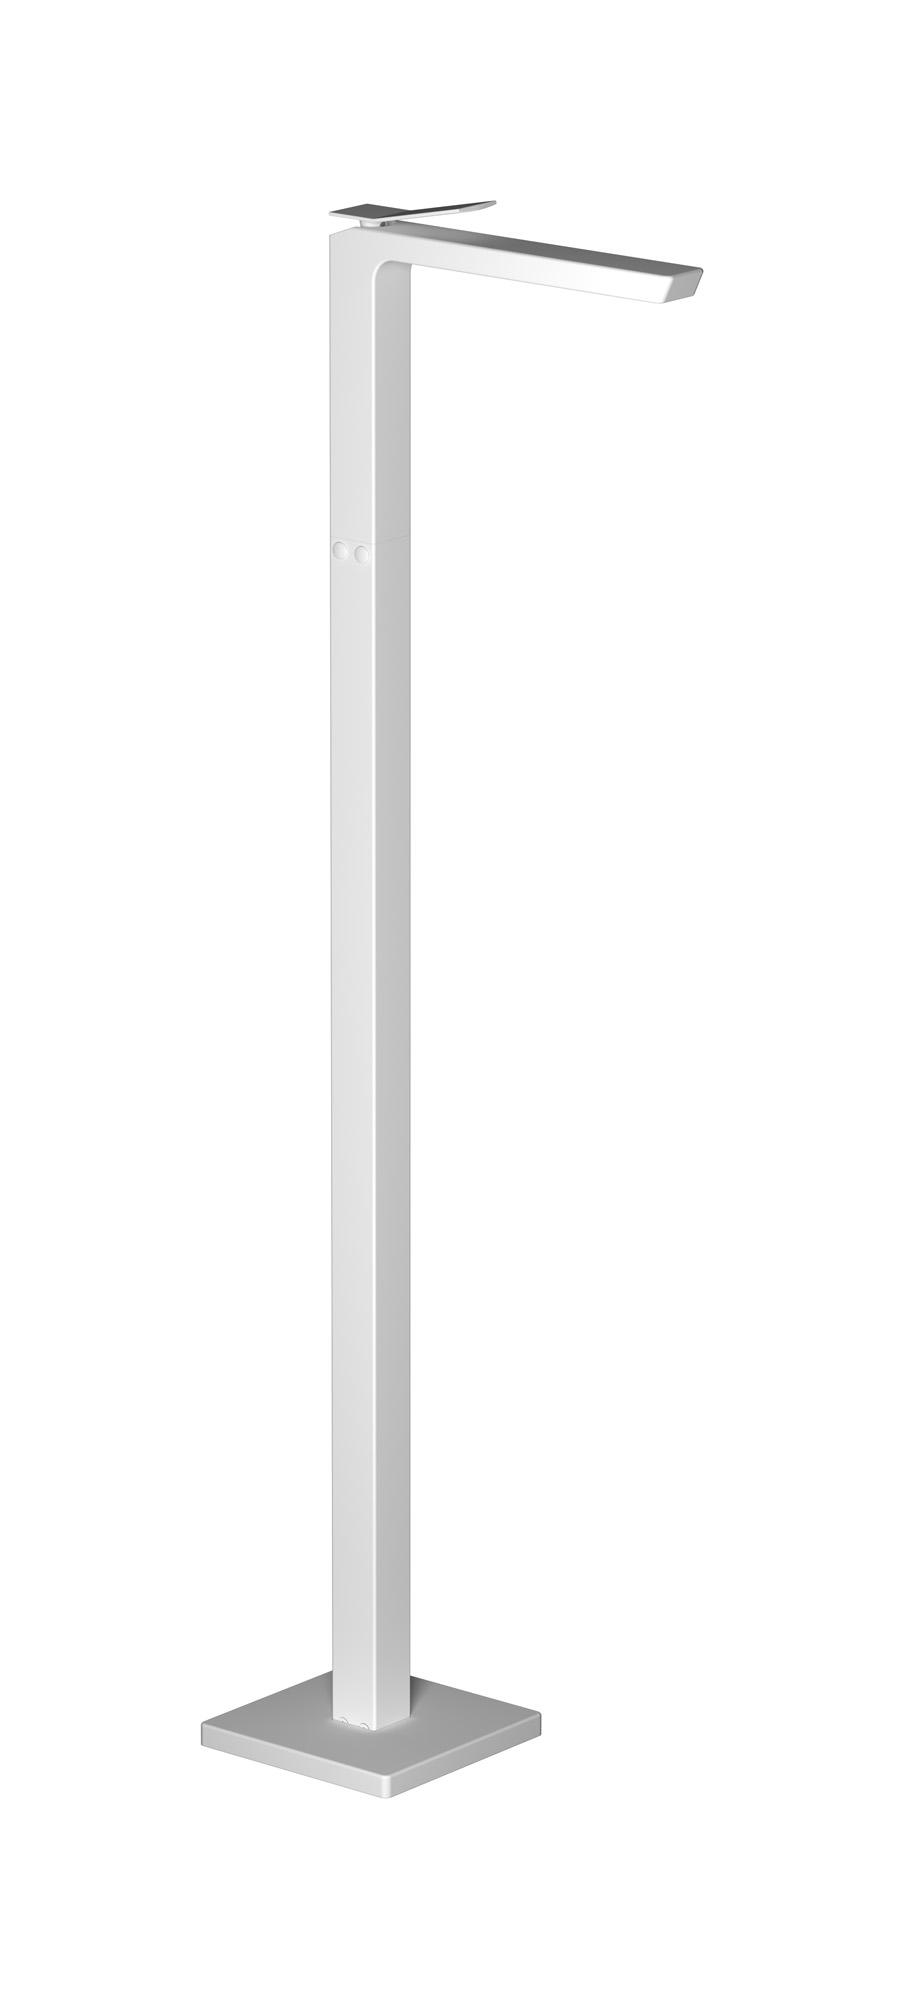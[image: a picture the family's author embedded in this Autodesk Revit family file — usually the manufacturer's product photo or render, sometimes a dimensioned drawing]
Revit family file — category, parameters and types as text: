
# Revit family: WA299
name_source: partatom
category: Apparecchi idraulici
units: mm (PartAtom-declared; Revit-internal decimal feet)

## family parameters
Basato su piano di lavoro = No
Condiviso = No
Mantieni orientamento annotazione = No
Numero OmniClass = 23.45.55.17
Punto di calcolo locali = No
Quota connettore circolare = Usa diametro
Sempre verticale = Sì
Taglio con vuoti quando caricato = No
Tipo di parte = Normale
Titolo OmniClass = Mixing Faucets

## types (12) — shared parameters
Cold water inlet = 10 mm  [stored 0.0328084 ft]
Commenti sul tipo = Washbasin mixer
Connessione CW = No
Connessione HW = No
Connessione di scarico = No
Connessione di ventilazione = No
Descrizione = Monohole freestanding washbasin mixer complete with drain
Hot water inlet = 10 mm  [stored 0.0328084 ft]
Produttore = IB Rubinetterie S.p.A.
URL = https://www.weareib.it
zero-valued in all types: Prospetto di default

## per-type parameters (varying)
| type | Finishes surface | Immagine tipo | Modello |
| Chrome | IB_Chrome | WA299CC.jpg | WA299CC |
| Brushed nickel | IB_Brushed nickel | WA299SS.jpg | WA299SS |
| Matt black | IB_matt black | WA299NP.jpg | WA299NP |
| Matt white | IB_matt white | WA299BO.jpg | WA299BO |
| Black chrome | IB_Black chrome | WA299CF.jpg | WA299CF |
| Brushed black chrome | IB_Brushed black chrome | WA299CS.jpg | WA299CS |
| Pale gold | IB_Pale gold | WA299II.jpg | WA299II |
| Brushed pale gold | IB_brushed pale gold | WA299IS.jpg | WA299IS |
| Rose gold | IB_Rose gold | WA299RS.jpg | WA299RS |
| Brushed rose gold | IB_Brushed rose gold | WA299SR.jpg | WA299SR |
| Gold | IB_gold | WA299OO.jpg | WA299OO |
| Brushed gold | IB_brushed gold | WA299OS.jpg | WA299OS |

note: [stored X ft] marks values corroborated as IEEE doubles in the binary element streams (Revit-internal decimal feet)
